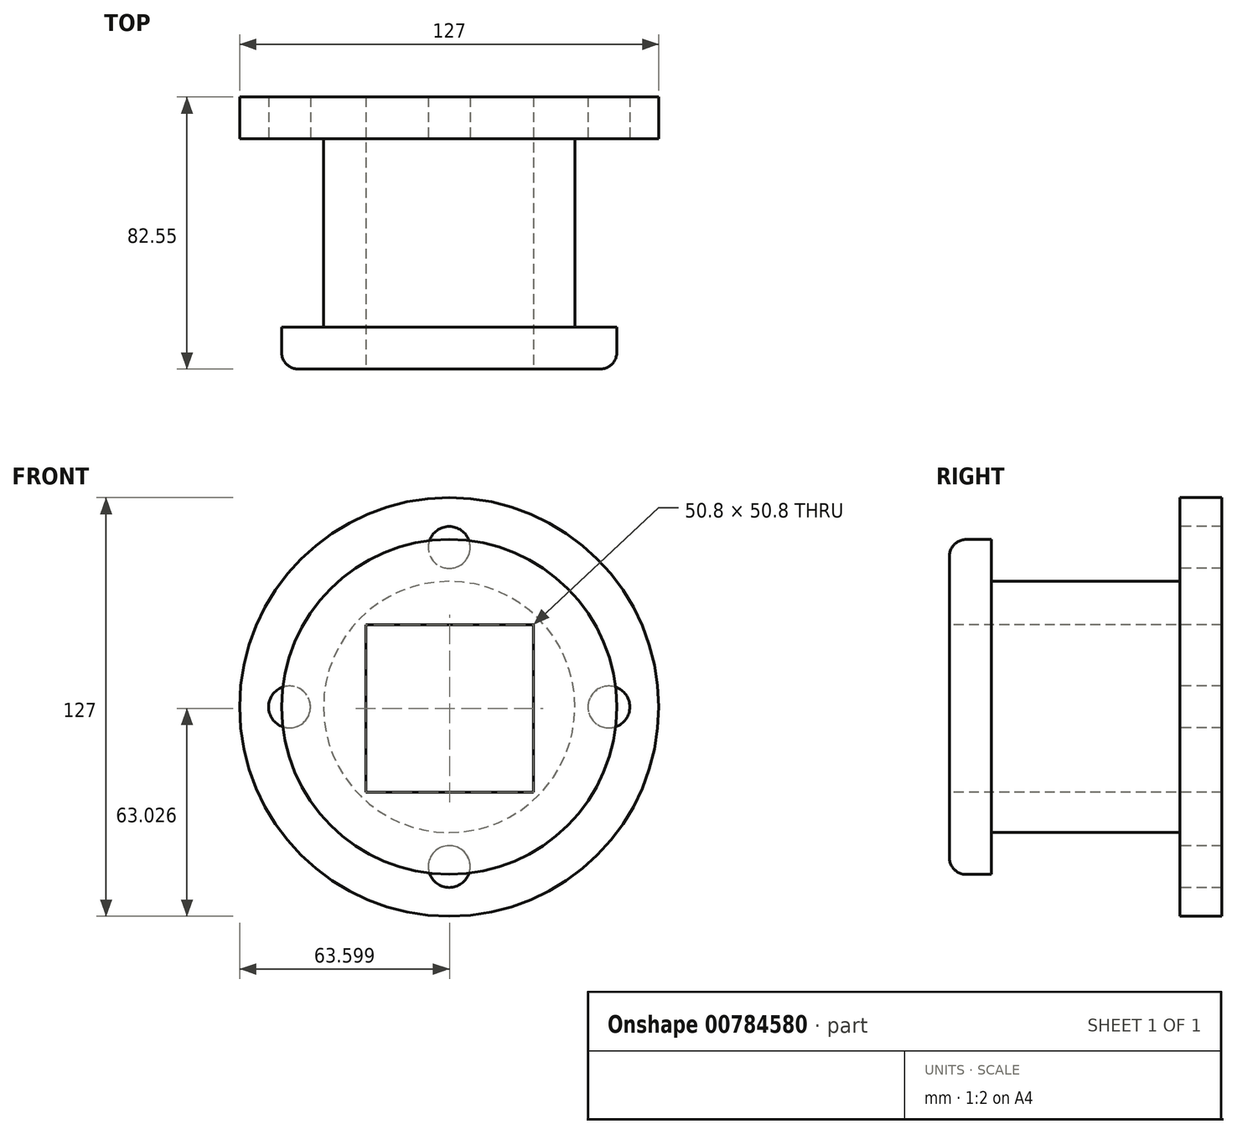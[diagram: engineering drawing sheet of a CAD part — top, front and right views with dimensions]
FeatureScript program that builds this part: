
annotation { "Feature Type Name" : "Feature", "Feature Type Description" : "" }
export const myFeature = defineFeature(function(context is Context, id is Id, definition is map)
    precondition{}
    {
        {
            var Q0;
            Q0=qCreatedBy(makeId("Front.planeOp"),FACE);
            var sketch = newSketch(context, id + "F0", { "sketchPlane" : qUnion([Q0])});
            skCircle(sketch, "E0", {"center": v(0, 0) * mm, "radius": 63.5 * mm});
            skSolve(sketch);
        }
        {
            var Q0;
            Q0=makeQuery(id+"F0.imprint","IMPRINT",FACE,{"disambiguationData":[TD([[makeQuery(id+"F0.imprint","IMPRINT",EDGE,{"derivedFrom":sQuery(id+"F0.wireOp",EDGE,"E0")}),1.0]])]});
            extrude(context, id + "F1", {"entities" : qUnion([Q0]), "depth" : 12.7 * mm, "offsetDistance" : 25.4 * mm});
        }
        {
            var Q0;
            Q0=makeQuery(id+"F1.opExtrude","CAP_FACE",FACE,{"disambiguationData":[OSD([sQuery(id+"F0.wireOp",EDGE,"E0")])],"isStart":false});
            var sketch = newSketch(context, id + "F2", { "sketchPlane" : qUnion([Q0])});
            skCircle(sketch, "E1", {"center": v(0, 0) * mm, "radius": 38.1 * mm});
            skSolve(sketch);
        }
        {
            var Q0;
            Q0=makeQuery(id+"F2.imprint","IMPRINT",FACE,{"disambiguationData":[TD([[makeQuery(id+"F2.imprint","IMPRINT",EDGE,{"derivedFrom":sQuery(id+"F2.wireOp",EDGE,"E1")}),1.0]])]});
            extrude(context, id + "F3", {"entities" : qUnion([Q0]), "operationType" : NewBodyOperationType.ADD, "depth" : 57.15 * mm, "offsetDistance" : 25.4 * mm});
        }
        {
            var Q0;
            Q0=makeQuery(id+"F3.opExtrude","CAP_FACE",FACE,{"disambiguationData":[OSD([sQuery(id+"F2.wireOp",EDGE,"E1")])],"isStart":false});
            var sketch = newSketch(context, id + "F4", { "sketchPlane" : qUnion([Q0])});
            skCircle(sketch, "E2", {"center": v(0, 0) * mm, "radius": 50.8 * mm});
            skSolve(sketch);
        }
        {
            var Q0;
            Q0=makeQuery(id+"F4.imprint","IMPRINT",FACE,{"disambiguationData":[TD([[makeQuery(id+"F4.imprint","IMPRINT",EDGE,{"derivedFrom":sQuery(id+"F4.wireOp",EDGE,"E2")}),1.0]])]});
            var Q1;
            Q1=makeQuery(id+"F4.imprint","IMPRINT",FACE,{"disambiguationData":[TD([[makeQuery(id+"F4.imprint","IMPRINT",EDGE,{"derivedFrom":makeQuery(id+"F3.opExtrude","CAP_EDGE",EDGE,{"disambiguationData":[OSD([sQuery(id+"F2.wireOp",EDGE,"E1")])],"isStart":false})}),1.0]])]});
            extrude(context, id + "F5", {"entities" : qUnion([Q0, Q1]), "operationType" : NewBodyOperationType.ADD, "depth" : 12.7 * mm, "offsetDistance" : 25.4 * mm});
        }
        {
            var Q0;
            Q0=makeQuery(id+"F5.opExtrude","CAP_FACE",FACE,{"disambiguationData":[OSD([sQuery(id+"F4.wireOp",EDGE,"E2")])],"isStart":false});
            fillet(context, id + "F6", {"entities" : qUnion([Q0]), "radius" : 5.08 * mm, "tangentPropagation" : true, "allowEdgeOverflow" : false});
        }
        {
            var Q0;
            Q0=makeQuery(id+"F1.opExtrude","CAP_FACE",FACE,{"disambiguationData":[OSD([sQuery(id+"F0.wireOp",EDGE,"E0")])],"isStart":false});
            var sketch = newSketch(context, id + "F7", { "sketchPlane" : qUnion([Q0])});
            skCircle(sketch, "E3", {"center": v(-48.4, 0) * mm, "radius": 6.35 * mm});
            skCircle(sketch, "E4.1.0", {"center": v(0, -48.4) * mm, "radius": 6.35 * mm});
            skCircle(sketch, "E4.2.0", {"center": v(48.4, 0) * mm, "radius": 6.35 * mm});
            skCircle(sketch, "E4.3.0", {"center": v(0, 48.4) * mm, "radius": 6.35 * mm});
            skPoint(sketch, "E4.center", {"position": v(0, 0) * mm});
            skSolve(sketch);
        }
        {
            var Q0;
            Q0 = qSketchRegion(id + "F7", true);
            extrude(context, id + "F8", {"entities" : qUnion([Q0]), "operationType" : NewBodyOperationType.REMOVE, "oppositeDirection" : true, "depth" : 12.7 * mm, "offsetDistance" : 25.4 * mm});
        }
        {
            var Q0;
            Q0=makeQuery(id+"F5.opExtrude","CAP_FACE",FACE,{"disambiguationData":[OSD([sQuery(id+"F4.wireOp",EDGE,"E2")])],"isStart":false});
            var sketch = newSketch(context, id + "F9", { "sketchPlane" : qUnion([Q0])});
            skLineSegment(sketch, "E5.bottom", {"start": v(25.5, -25.87) * mm, "end": v(-25.3, -25.87) * mm});
            skLineSegment(sketch, "E5.top", {"start": v(25.5, 24.93) * mm, "end": v(-25.3, 24.93) * mm});
            skLineSegment(sketch, "E5.left", {"start": v(25.5, -25.87) * mm, "end": v(25.5, 24.93) * mm});
            skLineSegment(sketch, "E5.right", {"start": v(-25.3, -25.87) * mm, "end": v(-25.3, 24.93) * mm});
            skSolve(sketch);
        }
        {
            var Q0;
            Q0=makeQuery(id+"F9.imprint","IMPRINT",FACE,{"disambiguationData":[TD([[makeQuery(id+"F9.imprint","IMPRINT",EDGE,{"derivedFrom":sQuery(id+"F9.wireOp",EDGE,"E5.bottom")}),-1.0]])]});
            extrude(context, id + "F10", {"entities" : qUnion([Q0]), "operationType" : NewBodyOperationType.REMOVE, "oppositeDirection" : true, "depth" : 127 * mm, "offsetDistance" : 25.4 * mm});
        }
    });
